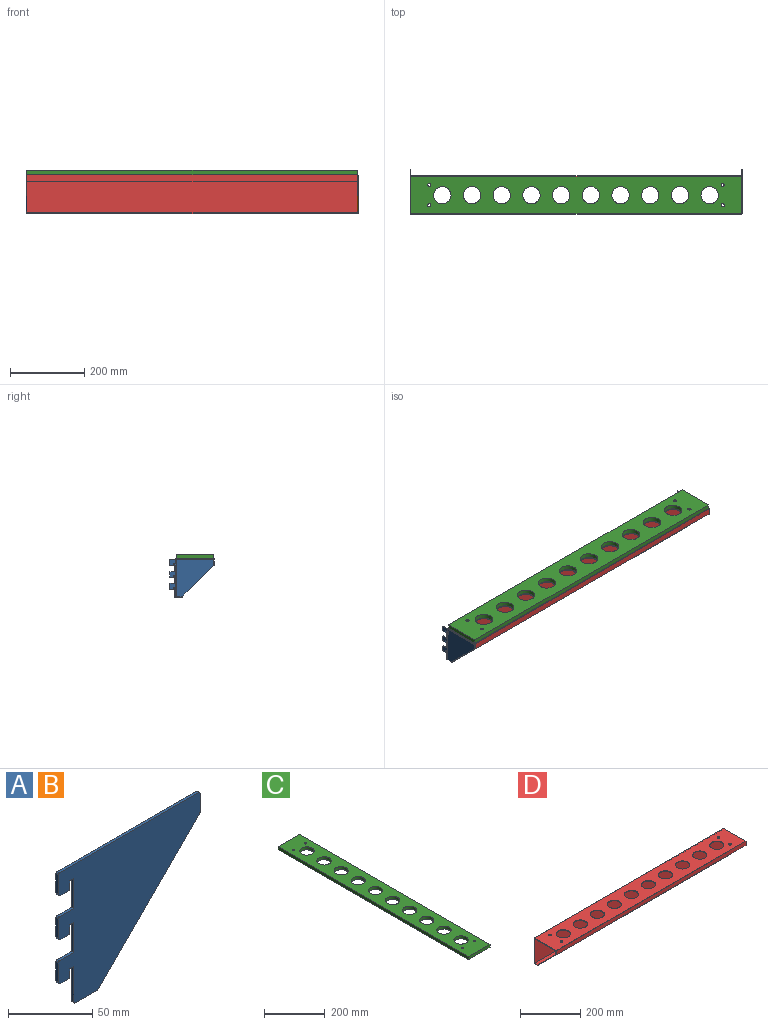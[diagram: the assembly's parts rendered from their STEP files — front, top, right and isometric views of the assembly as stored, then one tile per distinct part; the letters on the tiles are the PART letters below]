
ASSEMBLY  parts=4 mates=9
PART A: 36 faces, bbox 119x2x101 mm
  f0: plane 3.5x2mm, normal (0,0,-1), area 7mm2, adj f1,f9,f10,f26
  f1: plane 26x2mm, normal (-1,0,0), area 52mm2, adj f0,f9,f10,f35
  f2: plane 3.5x2mm, normal (0,0,-1), area 7mm2, adj f3,f9,f10,f20
  f3: plane 22x2mm, normal (-1,0,0), area 44mm2, adj f2,f9,f10,f23
  f4: plane 3.5x2mm, normal (0,0,-1), area 7mm2, adj f5,f9,f10,f14
  f5: plane 22x2mm, normal (-1,0,0), area 44mm2, adj f4,f9,f10,f17
  f6: plane 18.59x2mm, normal (0,0,-1), area 37.2mm2, adj f9,f10,f33,f35
  f7: plane 13.59x2mm, normal (1,0,0), area 27.2mm2, adj f9,f10,f32,f34
  f8: plane 117x2mm, normal (0,0,1), area 234mm2, adj f9,f10,f31,f34
  f9: plane 119x101mm, normal (0,1,0), area 7587.5mm2, adj f0,f1,f2,f3,f4,f5,f6,f7
  f10: plane 119x101mm, normal (0,-1,0), area 7587.5mm2, adj f0,f1,f2,f3,f4,f5,f6,f7
  f11: plane 85.41x85.41mm, normal (0.71,0,-0.71), area 241.6mm2, adj f9,f10,f32,f33
  f12: plane 13.8x2mm, normal (-1,0,0), area 27.6mm2, adj f9,f10,f15,f31
  f13: cylinder r=1mm len=2mm, axis (0,-1,0), area 3.1mm2, adj f9,f10,f14,f16
  f14: plane 5.8x2mm, normal (1,0,0), area 11.6mm2, adj f4,f9,f10,f13
  f15: cylinder r=2mm len=2mm, axis (0,-1,0), area 6.3mm2, adj f9,f10,f12,f16
  f16: plane 6.5x2mm, normal (0,0,-1), area 13mm2, adj f9,f10,f13,f15
  f17: plane 12x2mm, normal (0,0,1), area 24mm2, adj f5,f9,f10,f30
  f18: plane 13.8x2mm, normal (-1,0,0), area 27.6mm2, adj f9,f10,f21,f30
  f19: cylinder r=1mm len=2mm, axis (0,-1,0), area 3.1mm2, adj f9,f10,f20,f22
  f20: plane 5.8x2mm, normal (1,0,0), area 11.6mm2, adj f2,f9,f10,f19
  f21: cylinder r=2mm len=2mm, axis (0,-1,0), area 6.3mm2, adj f9,f10,f18,f22
  f22: plane 6.5x2mm, normal (0,0,-1), area 13mm2, adj f9,f10,f19,f21
  f23: plane 12x2mm, normal (0,0,1), area 24mm2, adj f3,f9,f10,f29
  f24: plane 13.8x2mm, normal (-1,0,0), area 27.6mm2, adj f9,f10,f27,f29
  f25: cylinder r=1mm len=2mm, axis (0,-1,0), area 3.1mm2, adj f9,f10,f26,f28
  f26: plane 5.8x2mm, normal (1,0,0), area 11.6mm2, adj f0,f9,f10,f25
  f27: cylinder r=2mm len=2mm, axis (0,-1,0), area 6.3mm2, adj f9,f10,f24,f28
  f28: plane 6.5x2mm, normal (0,0,-1), area 13mm2, adj f9,f10,f25,f27
  f29: cylinder r=1mm len=2mm, axis (0,-1,0), area 3.1mm2, adj f9,f10,f23,f24
  f30: cylinder r=1mm len=2mm, axis (0,-1,0), area 3.1mm2, adj f9,f10,f17,f18
  f31: cylinder r=1mm len=2mm, axis (0,-1,0), area 3.1mm2, adj f8,f9,f10,f12
  f32: cylinder r=1mm len=2mm, axis (0,1,0), area 1.6mm2, adj f7,f9,f10,f11
  f33: cylinder r=1mm len=2mm, axis (0,-1,0), area 1.6mm2, adj f6,f9,f10,f11
  f34: cylinder r=1mm len=2mm, axis (0,-1,0), area 3.1mm2, adj f7,f8,f9,f10
  f35: cylinder r=1mm len=2mm, axis (0,-1,0), area 3.1mm2, adj f1,f6,f9,f10
PART B: same geometry as A
PART C: 20 faces, bbox 100x890x12 mm
  f0: plane 890x100mm, normal (0,0,-1), area 71423.6mm2, adj f1,f3,f4,f5,f6,f7,f8,f9
  f1: plane 890x12mm, normal (1,0,0), area 10680mm2, adj f0,f2,f4,f5
  f2: plane 890x100mm, normal (0,0,1), area 71423.6mm2, adj f1,f3,f4,f5,f6,f7,f8,f9
  f3: plane 890x12mm, normal (-1,0,0), area 10680mm2, adj f0,f2,f4,f5
  f4: plane 100x12mm, normal (0,1,0), area 1200mm2, adj f0,f1,f2,f3
  f5: plane 100x12mm, normal (0,-1,0), area 1200mm2, adj f0,f1,f2,f3
  f6: cylinder r=23.5mm len=47mm, axis (0,0,1), area 1771.9mm2, adj f0,f2
  f7: cylinder r=23.5mm len=47mm, axis (0,0,1), area 1771.9mm2, adj f0,f2
  f8: cylinder r=23.5mm len=47mm, axis (0,0,1), area 1771.9mm2, adj f0,f2
  f9: cylinder r=23.5mm len=47mm, axis (0,0,1), area 1771.9mm2, adj f0,f2
  f10: cylinder r=23.5mm len=47mm, axis (0,0,1), area 1771.9mm2, adj f0,f2
  f11: cylinder r=23.5mm len=47mm, axis (0,0,1), area 1771.9mm2, adj f0,f2
  f12: cylinder r=23.5mm len=47mm, axis (0,0,1), area 1771.9mm2, adj f0,f2
  f13: cylinder r=23.5mm len=47mm, axis (0,0,1), area 1771.9mm2, adj f0,f2
  f14: cylinder r=23.5mm len=47mm, axis (0,0,1), area 1771.9mm2, adj f0,f2
  f15: cylinder r=23.5mm len=47mm, axis (0,0,1), area 1771.9mm2, adj f0,f2
  f16: cylinder r=4.25mm len=12mm, axis (0,0,1), area 320.4mm2, adj f0,f2
  f17: cylinder r=4.25mm len=12mm, axis (0,0,1), area 320.4mm2, adj f0,f2
  f18: cylinder r=4.25mm len=12mm, axis (0,0,1), area 320.4mm2, adj f0,f2
  f19: cylinder r=4.25mm len=12mm, axis (0,0,1), area 320.4mm2, adj f0,f2
PART D: 26 faces, bbox 890x104x104 mm
  f0: plane 890x100mm, normal (0,-1,0), area 89000mm2, adj f1,f2,f4,f11
  f1: plane 890x100mm, normal (0,0,-1), area 71423.6mm2, adj f0,f2,f4,f8,f12,f13,f14,f15
  f2: plane 104x104mm, normal (-1,0,0), area 472mm2, adj f0,f1,f3,f5,f6,f7,f8,f9
  f3: plane 890x17mm, normal (0,-1,0), area 15130mm2, adj f2,f4,f6,f7
  f4: plane 104x104mm, normal (1,0,0), area 472mm2, adj f0,f1,f3,f5,f6,f7,f8,f9
  f5: plane 890x104mm, normal (0,1,0), area 92560mm2, adj f2,f4,f6,f9
  f6: plane 890x104mm, normal (0,0,1), area 74983.6mm2, adj f2,f3,f4,f5,f12,f13,f14,f15
  f7: plane 890x2mm, normal (0,0,-1), area 1780mm2, adj f2,f3,f4,f8
  f8: plane 890x15mm, normal (0,1,0), area 13350mm2, adj f1,f2,f4,f7
  f9: plane 890x17mm, normal (0,0,-1), area 15130mm2, adj f2,f4,f5,f10
  f10: plane 890x2mm, normal (0,-1,0), area 1780mm2, adj f2,f4,f9,f11
  f11: plane 890x15mm, normal (0,0,1), area 13350mm2, adj f0,f2,f4,f10
  f12: cylinder r=23.5mm len=47mm, axis (0,0,1), area 295.3mm2, adj f1,f6
  f13: cylinder r=23.5mm len=47mm, axis (0,0,1), area 295.3mm2, adj f1,f6
  f14: cylinder r=23.5mm len=47mm, axis (0,0,1), area 295.3mm2, adj f1,f6
  f15: cylinder r=23.5mm len=47mm, axis (0,0,1), area 295.3mm2, adj f1,f6
  f16: cylinder r=23.5mm len=47mm, axis (0,0,1), area 295.3mm2, adj f1,f6
  f17: cylinder r=23.5mm len=47mm, axis (0,0,1), area 295.3mm2, adj f1,f6
  f18: cylinder r=23.5mm len=47mm, axis (0,0,1), area 295.3mm2, adj f1,f6
  f19: cylinder r=23.5mm len=47mm, axis (0,0,1), area 295.3mm2, adj f1,f6
  f20: cylinder r=23.5mm len=47mm, axis (0,0,1), area 295.3mm2, adj f1,f6
  f21: cylinder r=23.5mm len=47mm, axis (0,0,1), area 295.3mm2, adj f1,f6
  f22: cylinder r=4.25mm len=8.5mm, axis (0,0,1), area 53.4mm2, adj f1,f6
  f23: cylinder r=4.25mm len=8.5mm, axis (0,0,1), area 53.4mm2, adj f1,f6
  f24: cylinder r=4.25mm len=8.5mm, axis (0,0,1), area 53.4mm2, adj f1,f6
  f25: cylinder r=4.25mm len=8.5mm, axis (0,0,1), area 53.4mm2, adj f1,f6
PLACE A rot(axis=(0,0,-1),90deg) t=(-892,2,-101)mm
PLACE B rot(axis=(0,0,-1),90deg) t=(0,2,-101)mm
PLACE C rot(axis=(0,0,1),90deg) t=(0,102,2)mm
PLACE D at identity fixed
MATE cylindrical C.f15 <-> D.f12  axis (0,0,1) through (-805,52,8)mm
MATE planar D.f6 <-> C.f0  axis (0,0,1) through (0,52,2)mm
MATE planar B.f8 <-> D.f1  axis (0,0,1) through (1,61.5,0)mm
MATE planar D.f4 <-> B.f10  axis (1,0,0) through (0,73.5,-28.5)mm
MATE planar D.f2 <-> A.f9  axis (-1,0,0) through (-890,73.5,-28.5)mm
MATE planar A.f7 <-> B.f7  axis (0,-1,0) through (-891,2,-7.79)mm
MATE planar B.f8 <-> A.f8  axis (0,0,1) through (1,61.5,0)mm
MATE planar B.f7 <-> D.f8  axis (0,-1,0) through (1,2,-7.79)mm
MATE cylindrical C.f6 <-> D.f21  axis (0,0,1) through (-85,52,14)mm
